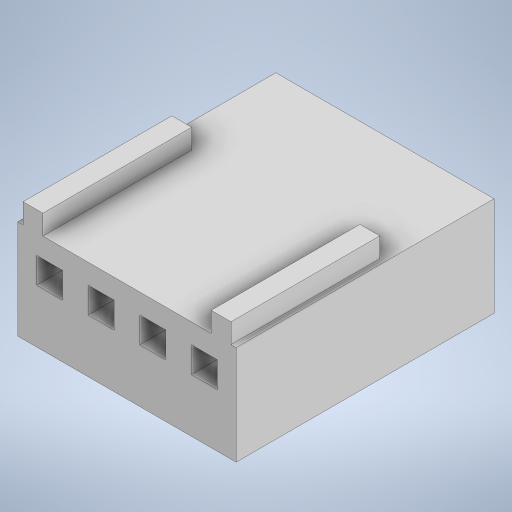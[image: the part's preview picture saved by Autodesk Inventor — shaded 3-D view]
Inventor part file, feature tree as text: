
AUTODESK INVENTOR PART (.ipt)
format: ipt  version: 2023 (Build 270158000, 158)  size: 258,560 bytes
history: native  units: mm
features: extrude x3, sketch x3
ambient origin geometry x8: Origin, YZ Plane, XZ Plane, XY Plane, X Axis, Y Axis, Z Axis, Center Point
bodies: Solid1 (feature_tree)
feature tree (6):
  extrude  "Extrusion1"  Depth=5.5mm
  extrude  "Extrusion2"  Depth=6.5mm
  extrude  "Extrusion3"  Depth=0.26mm
  sketch  "Sketch1"  dims[d0=11.0mm d1=5.5mm]
  sketch  "Sketch2"  dims[d2=13.0mm d3=6.5mm]
  sketch  "Sketch3"  dims[d4=5.0mm d5=0.0mm d6=0.26mm d7=0.26mm d8=1.0mm d9=1.0mm d10=7.5mm d11=7.5mm d12=1.0mm d13=0.0mm d14=1.3mm d15=1.3mm d18=1.3mm d19=1.3mm d21=1.3mm d22=1.3mm d23=1.3mm d24=0.65mm d25=1.3mm d26=1.0mm d27=1.0mm d28=0.0mm]
